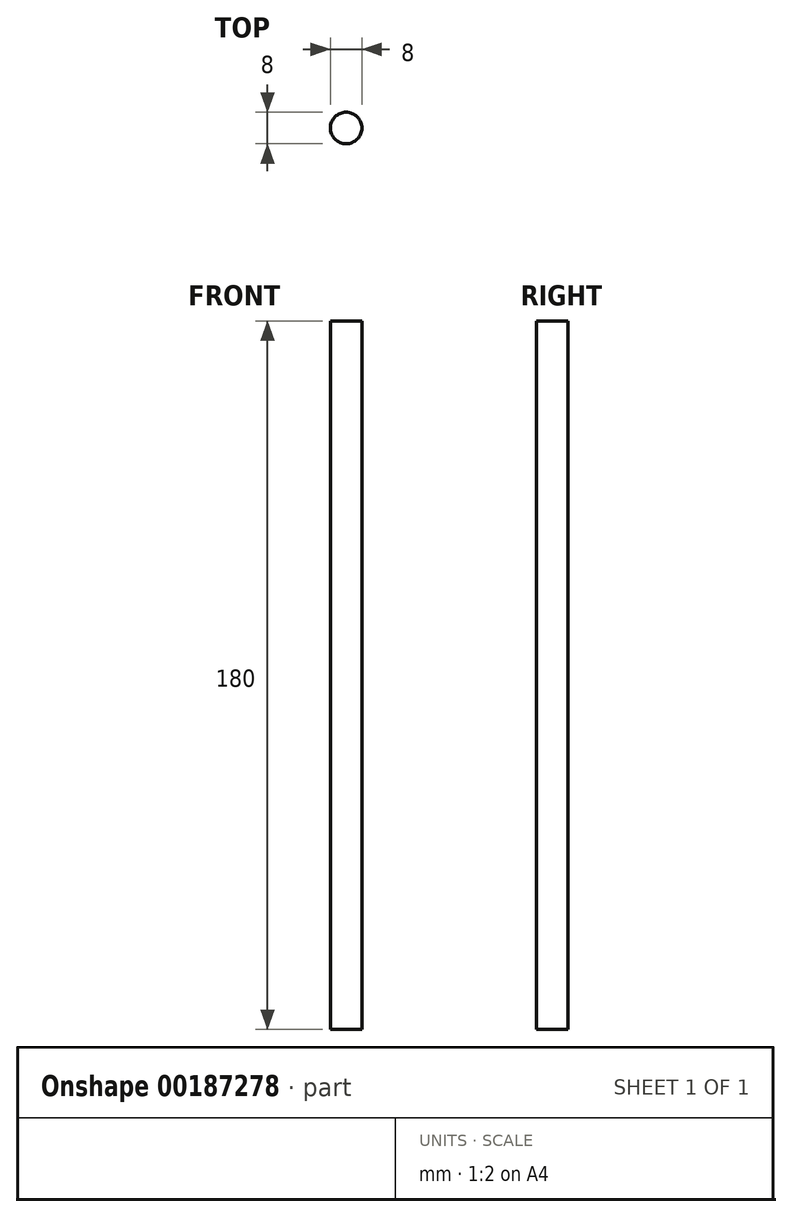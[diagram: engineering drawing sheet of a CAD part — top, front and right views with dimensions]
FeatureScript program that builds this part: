
annotation { "Feature Type Name" : "Feature", "Feature Type Description" : "" }
export const myFeature = defineFeature(function(context is Context, id is Id, definition is map)
    precondition{}
    {
        {
            var Q0;
            Q0=qCreatedBy(makeId("Top.planeOp"),FACE);
            var sketch = newSketch(context, id + "F0", { "sketchPlane" : qUnion([Q0])});
            skCircle(sketch, "E0", {"center": v(0, 0) * mm, "radius": 4 * mm});
            skSolve(sketch);
        }
        {
            var Q0;
            Q0=makeQuery(id+"F0.imprint","IMPRINT",FACE,{"disambiguationData":[TD([[makeQuery(id+"F0.imprint","IMPRINT",EDGE,{"derivedFrom":sQuery(id+"F0.wireOp",EDGE,"E0")}),1.0]])]});
            extrude(context, id + "F1", {"entities" : qUnion([Q0]), "depth" : 180 * mm, "offsetDistance" : 25 * mm});
        }
    });
